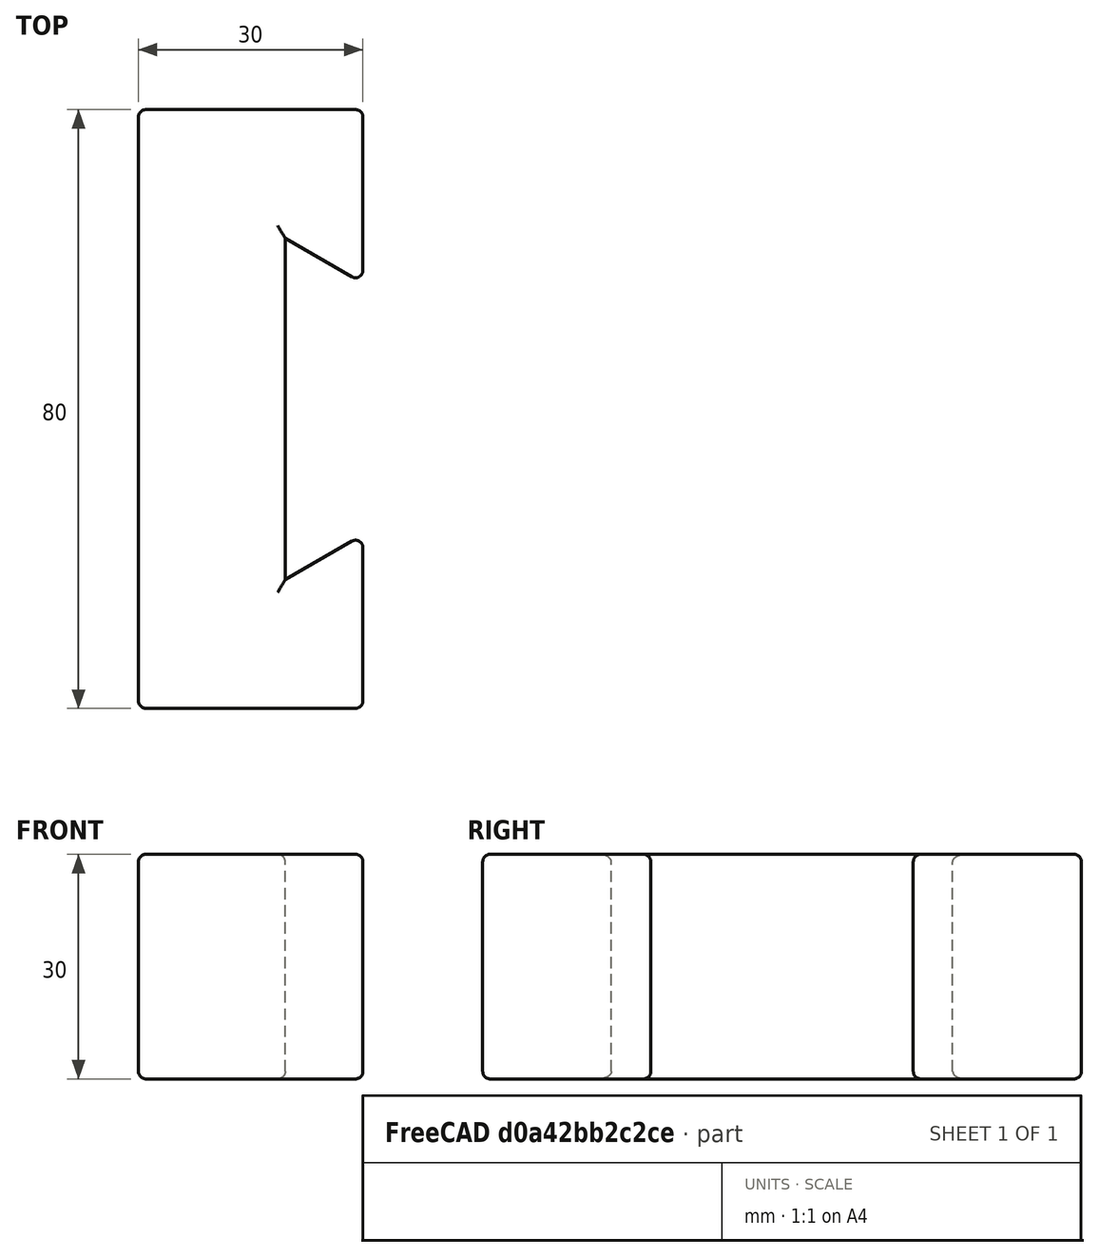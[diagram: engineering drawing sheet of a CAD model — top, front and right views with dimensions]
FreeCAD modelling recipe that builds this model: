
FCSTD DOCUMENT  (FreeCAD 0.16R)
Label: BXA3
License: All rights reserved
LicenseURL: http://en.wikipedia.org/wiki/All_rights_reserved
objects: Sketcher::SketchObject×1, PartDesign::Pad×1, PartDesign::Fillet×1, Mesh::Feature×1
note: 4 computed .brp shape members not serialized (recipe doc carries the construction recipe); baked Part::Feature solids carry a one-line shape summary decoded from their .brp

FEATURE [Sketcher::SketchObject] Sketch
  sketch-geometry (8):
    g0: LineSegment StartX=0 StartY=16.8 StartZ=0 EndX=0 EndY=40 EndZ=0
    g1: LineSegment StartX=0 StartY=40 StartZ=0 EndX=-30 EndY=40 EndZ=0
    g2: LineSegment StartX=-30 StartY=40 StartZ=0 EndX=-30 EndY=-40 EndZ=0
    g3: LineSegment StartX=-30 StartY=-40 StartZ=0 EndX=0 EndY=-40 EndZ=0
    g4: LineSegment StartX=0 StartY=-40 StartZ=0 EndX=0 EndY=-16.8 EndZ=0
    g5: LineSegment StartX=0 StartY=-16.8 StartZ=0 EndX=-10.39 EndY=-22.7987 EndZ=0
    g6: LineSegment StartX=-10.39 StartY=-22.7987 StartZ=0 EndX=-10.39 EndY=22.7987 EndZ=0
    g7: LineSegment StartX=-10.39 StartY=22.7987 StartZ=0 EndX=0 EndY=16.8 EndZ=0
  constraints (24):
    c: Coincident(g0,g1)
    c: Coincident(g1,g2)
    c: Vertical(g2)
    c: Coincident(g2,g3)
    c: Horizontal(g3)
    c: Coincident(g3,g4)
    c: Vertical(g4)
    c: Coincident(g4,g5)
    c: Coincident(g5,g6)
    c: Coincident(g6,g7)
    c: Vertical(g0)
    c: Horizontal(g1)
    c: Vertical(g6)
    c: Coincident(g7,g0)
    c: DistanceY(g4,g0) = 33.6
    c: Symmetric(g4,g0,g-1)
    c: Symmetric(g5,g6,g-1)
    c: Symmetric(g3,g0,g-1)
    c: DistanceX(g1,g1) = 30
    c: DistanceY(g2,g2) = 80
    c: Angle(g7) = -0.523599
    c: Angle(g5) = -2.61799
    c: PointOnObject(g4,g-2)
    c: DistanceX(g6,g0) = 10.39
FEATURE [PartDesign::Pad] Pad
  Length = 30
  Length2 = 100
  Sketch = -> Sketch
  Type = 0
FEATURE [PartDesign::Fillet] Fillet
  Base = -> Pad [Edge4,Edge7,Edge10,Edge13,Edge16,Edge19,Edge22,Edge24,Edge1,Edge2,Edge3,Edge11,Edge14,Edge15,Edge6,Edge9,Edge12,Edge18,Edge21,Edge23,Edge8,Edge5]
  Radius = 1
FEATURE [Mesh::Feature] Mesh  label="Fillet (Meshed)"
